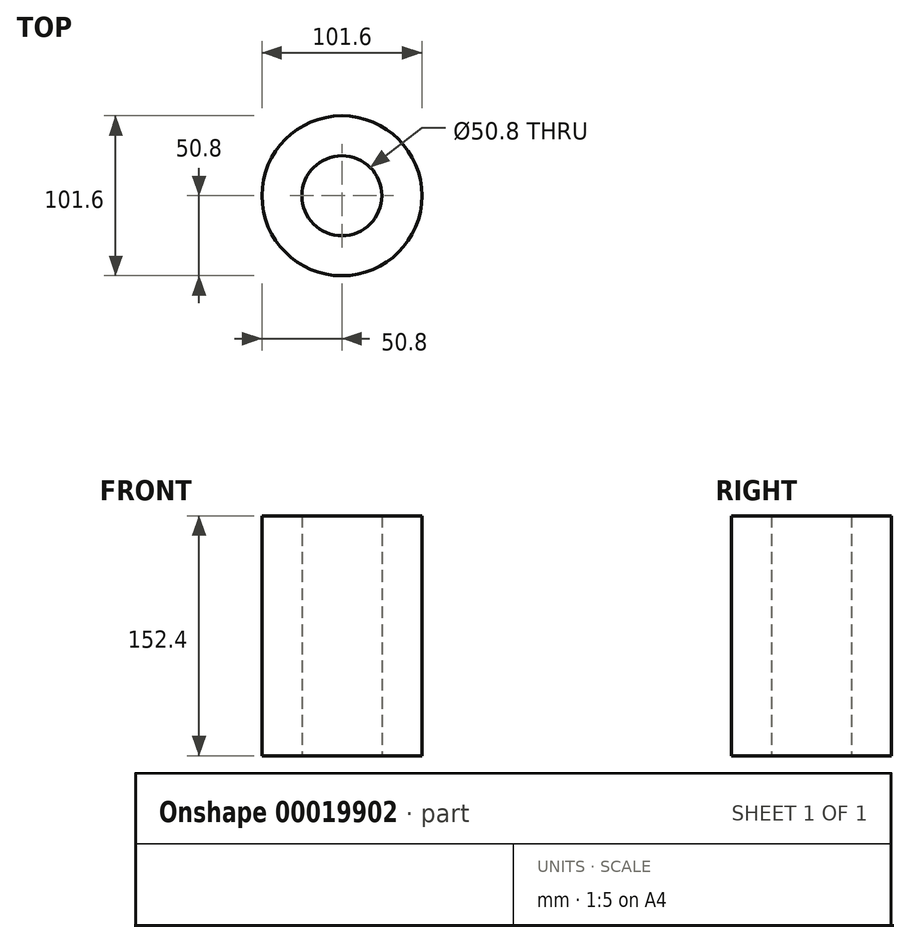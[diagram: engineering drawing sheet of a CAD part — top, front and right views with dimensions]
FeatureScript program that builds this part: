
annotation { "Feature Type Name" : "Feature", "Feature Type Description" : "" }
export const myFeature = defineFeature(function(context is Context, id is Id, definition is map)
    precondition{}
    {
        {
            var Q0;
            Q0=qCreatedBy(makeId("Top.planeOp"),FACE);
            var sketch = newSketch(context, id + "F0", { "sketchPlane" : qUnion([Q0])});
            skCircle(sketch, "E0", {"center": v(0, 0) * mm, "radius": 25.4 * mm});
            skCircle(sketch, "E1", {"center": v(0, 0) * mm, "radius": 50.8 * mm});
            skSolve(sketch);
        }
        {
            var Q0;
            Q0 = qSketchRegion(id + "F0", true);
            extrude(context, id + "F1", {"entities" : qUnion([Q0]), "depth" : 152.4 * mm});
        }
    });
